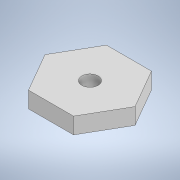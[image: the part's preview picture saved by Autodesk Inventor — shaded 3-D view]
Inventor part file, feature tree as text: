
AUTODESK INVENTOR PART (.ipt)
format: ipt  version: 2022 (Build 260153000, 153)  size: 96,768 bytes
history: native  units: mm
features: extrude x1, sketch x1
ambient origin geometry x8: Origin, YZ Plane, XZ Plane, XY Plane, X Axis, Y Axis, Z Axis, Center Point
bodies: Solid1 (feature_tree)
feature tree (2):
  extrude  "Extrusion1"  Depth=50.0mm TaperAngle=0.0deg
  sketch  "Sketch1"  dims[d0=120.0mm d1=50.0mm d2=0.0mm]
